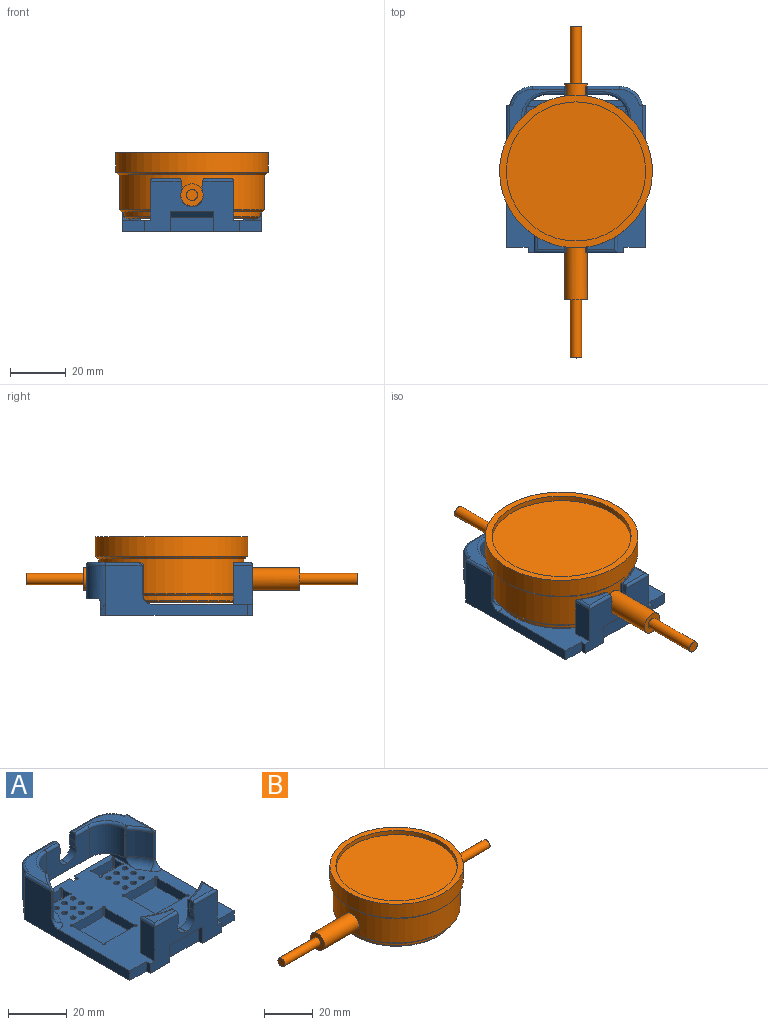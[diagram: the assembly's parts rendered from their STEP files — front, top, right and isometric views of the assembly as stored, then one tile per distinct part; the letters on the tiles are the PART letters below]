
ASSEMBLY  parts=2 mates=1
PART A: 181 faces, bbox 61.3x61.3x19.5 mm
  f0: plane 7x2mm, normal (-1,0,0), area 12mm2, adj f1,f6,f11,f135
  f1: plane 15.6x5mm, normal (0,-1,0), area 78mm2, adj f0,f7,f11,f135
  f2: plane 54.8x50mm, normal (0,0,1), area 1669.8mm2, adj f3,f4,f5,f6,f8,f9,f12,f32
  f3: plane 50.8x18mm, normal (-1,0,0), area 387.9mm2, adj f2,f4,f10,f11,f138,f142,f165
  f4: plane 7.8x4mm, normal (0,-1,0), area 31.2mm2, adj f2,f3,f5,f11
  f5: plane 4x2mm, normal (-1,0,0), area 8mm2, adj f2,f4,f6,f11
  f6: plane 34.4x18mm, normal (0,-1,0), area 383.7mm2, adj f0,f2,f5,f7,f11,f61,f113,f117
  f7: plane 7x2mm, normal (1,0,0), area 12mm2, adj f1,f6,f11,f135
  f8: plane 4.3x4mm, normal (0,1,0), area 13.2mm2, adj f2,f11,f12,f64
  f9: plane 22.09x5mm, normal (0,1,0), area 90.6mm2, adj f2,f11,f12,f13,f125,f153,f174
  f10: plane 19.09x2.26mm, normal (0,1,0), area 23.9mm2, adj f3,f11,f13,f123,f153,f165,f171
  f11: plane 54.8x50mm, normal (0,0,-1), area 2572mm2, adj f0,f1,f3,f4,f5,f6,f7,f8
  f12: plane 4x2mm, normal (0.97,0,-0.24), area 8.2mm2, adj f2,f8,f9,f11
  f13: plane 4x2mm, normal (-0.97,0,-0.24), area 6.1mm2, adj f9,f10,f11,f153
  f14: cylinder r=1.25mm len=2.5mm, axis (0,0,-1), area 11.8mm2, adj f11,f15
  f15: plane 2.5x2.5mm, normal (0,0,-1), area 1.8mm2, adj f14,f40
  f16: cylinder r=1.25mm len=2.5mm, axis (0,0,-1), area 11.8mm2, adj f11,f17
  f17: plane 2.5x2.5mm, normal (0,0,-1), area 1.8mm2, adj f16,f39
  f18: cylinder r=1.25mm len=2.5mm, axis (0,0,-1), area 11.8mm2, adj f11,f19
  f19: plane 2.5x2.5mm, normal (0,0,-1), area 1.8mm2, adj f18,f38
  f20: cylinder r=1.25mm len=2.5mm, axis (0,0,-1), area 11.8mm2, adj f11,f21
  f21: plane 2.5x2.5mm, normal (0,0,-1), area 1.8mm2, adj f20,f37
  f22: cylinder r=1.25mm len=2.5mm, axis (0,0,-1), area 11.8mm2, adj f11,f23
  f23: plane 2.5x2.5mm, normal (0,0,-1), area 1.8mm2, adj f22,f36
  f24: cylinder r=1.25mm len=2.5mm, axis (0,0,-1), area 11.8mm2, adj f11,f25
  f25: plane 2.5x2.5mm, normal (0,0,-1), area 1.8mm2, adj f24,f35
  f26: cylinder r=1.25mm len=2.5mm, axis (0,0,-1), area 11.8mm2, adj f11,f27
  f27: plane 2.5x2.5mm, normal (0,0,-1), area 1.8mm2, adj f26,f34
  f28: cylinder r=1.25mm len=2.5mm, axis (0,0,-1), area 11.8mm2, adj f11,f29
  f29: plane 2.5x2.5mm, normal (0,0,-1), area 1.8mm2, adj f28,f33
  f30: cylinder r=1.25mm len=2.5mm, axis (0,0,-1), area 11.8mm2, adj f11,f31
  f31: plane 2.5x2.5mm, normal (0,0,-1), area 1.8mm2, adj f30,f32
  f32: cylinder r=1mm len=2.5mm, axis (0,0,-1), area 15.7mm2, adj f2,f31
  f33: cylinder r=1mm len=2.5mm, axis (0,0,-1), area 15.7mm2, adj f2,f29
  f34: cylinder r=1mm len=2.5mm, axis (0,0,-1), area 15.7mm2, adj f2,f27
  f35: cylinder r=1mm len=2.5mm, axis (0,0,-1), area 15.7mm2, adj f2,f25
  f36: cylinder r=1mm len=2.5mm, axis (0,0,-1), area 15.7mm2, adj f2,f23
  f37: cylinder r=1mm len=2.5mm, axis (0,0,-1), area 15.7mm2, adj f2,f21
  f38: cylinder r=1mm len=2.5mm, axis (0,0,-1), area 15.7mm2, adj f2,f19
  f39: cylinder r=1mm len=2.5mm, axis (0,0,-1), area 15.7mm2, adj f2,f17
  f40: cylinder r=1mm len=2.5mm, axis (0,0,-1), area 15.7mm2, adj f2,f15
  f41: cylinder r=0.5mm len=3.8mm, axis (0,0,1), area 9mm2, adj f2,f42,f48,f49
  f42: plane 9.35x3.8mm, normal (0,1,0), area 35.5mm2, adj f2,f41,f43,f49
  f43: cylinder r=0.5mm len=3.8mm, axis (0,0,1), area 9mm2, adj f2,f42,f44,f49
  f44: plane 3.8x3.35mm, normal (-1,0,0), area 12.7mm2, adj f2,f43,f45,f49
  f45: cylinder r=0.5mm len=3.8mm, axis (0,0,1), area 9mm2, adj f2,f44,f46,f49
  f46: plane 9.35x3.8mm, normal (0,-1,0), area 35.5mm2, adj f2,f45,f47,f49
  f47: cylinder r=0.5mm len=3.8mm, axis (0,0,1), area 9mm2, adj f2,f46,f48,f49
  f48: plane 3.8x3.35mm, normal (1,0,0), area 12.7mm2, adj f2,f41,f47,f49
  f49: plane 11.35x5.35mm, normal (0,0,1), area 47.4mm2, adj f41,f42,f43,f44,f45,f46,f47,f48
  f50: cylinder r=0.5mm len=3.8mm, axis (0,0,1), area 9mm2, adj f2,f51,f57,f58
  f51: plane 14.35x3.8mm, normal (1,0,0), area 54.5mm2, adj f2,f50,f52,f58
  f52: cylinder r=0.5mm len=3.8mm, axis (0,0,1), area 9mm2, adj f2,f51,f53,f58
  f53: plane 14.35x3.8mm, normal (0,1,0), area 54.5mm2, adj f2,f52,f54,f58
  f54: cylinder r=0.5mm len=3.8mm, axis (0,0,1), area 9mm2, adj f2,f53,f55,f58
  f55: plane 14.35x3.8mm, normal (-1,0,0), area 54.5mm2, adj f2,f54,f56,f58
  f56: cylinder r=0.5mm len=3.8mm, axis (0,0,1), area 9mm2, adj f2,f55,f57,f58
  f57: plane 14.35x3.8mm, normal (0,-1,0), area 54.5mm2, adj f2,f50,f56,f58
  f58: plane 16.35x16.35mm, normal (0,0,1), area 238mm2, adj f50,f51,f52,f53,f54,f55,f56,f57
  f59: plane 50.8x18mm, normal (1,0,0), area 387.9mm2, adj f2,f11,f60,f63,f137,f140,f158
  f60: plane 7.8x4mm, normal (0,-1,0), area 31.2mm2, adj f2,f11,f59,f61
  f61: plane 4x2mm, normal (1,0,0), area 8mm2, adj f2,f6,f11,f60
  f62: plane 22.09x5mm, normal (0,1,0), area 90.6mm2, adj f2,f11,f64,f65,f122,f154,f173
  f63: plane 19.09x2.26mm, normal (0,1,0), area 23.9mm2, adj f11,f59,f65,f120,f154,f158,f169
  f64: plane 4x2mm, normal (-0.97,0,-0.24), area 8.2mm2, adj f2,f8,f11,f62
  f65: plane 4x2mm, normal (0.97,0,-0.24), area 6.1mm2, adj f11,f62,f63,f154
  f66: cylinder r=1.25mm len=2.5mm, axis (0,0,-1), area 11.8mm2, adj f11,f67
  f67: plane 2.5x2.5mm, normal (0,0,-1), area 1.8mm2, adj f66,f92
  f68: cylinder r=1.25mm len=2.5mm, axis (0,0,-1), area 11.8mm2, adj f11,f69
  f69: plane 2.5x2.5mm, normal (0,0,-1), area 1.8mm2, adj f68,f91
  f70: cylinder r=1.25mm len=2.5mm, axis (0,0,-1), area 11.8mm2, adj f11,f71
  f71: plane 2.5x2.5mm, normal (0,0,-1), area 1.8mm2, adj f70,f90
  f72: cylinder r=1.25mm len=2.5mm, axis (0,0,-1), area 11.8mm2, adj f11,f73
  f73: plane 2.5x2.5mm, normal (0,0,-1), area 1.8mm2, adj f72,f89
  f74: cylinder r=1.25mm len=2.5mm, axis (0,0,-1), area 11.8mm2, adj f11,f75
  f75: plane 2.5x2.5mm, normal (0,0,-1), area 1.8mm2, adj f74,f88
  f76: cylinder r=1.25mm len=2.5mm, axis (0,0,-1), area 11.8mm2, adj f11,f77
  f77: plane 2.5x2.5mm, normal (0,0,-1), area 1.8mm2, adj f76,f87
  f78: cylinder r=1.25mm len=2.5mm, axis (0,0,-1), area 11.8mm2, adj f11,f79
  f79: plane 2.5x2.5mm, normal (0,0,-1), area 1.8mm2, adj f78,f86
  f80: cylinder r=1.25mm len=2.5mm, axis (0,0,-1), area 11.8mm2, adj f11,f81
  f81: plane 2.5x2.5mm, normal (0,0,-1), area 1.8mm2, adj f80,f85
  f82: cylinder r=1.25mm len=2.5mm, axis (0,0,-1), area 11.8mm2, adj f11,f83
  f83: plane 2.5x2.5mm, normal (0,0,-1), area 1.8mm2, adj f82,f84
  f84: cylinder r=1mm len=2.5mm, axis (0,0,-1), area 15.7mm2, adj f2,f83
  f85: cylinder r=1mm len=2.5mm, axis (0,0,-1), area 15.7mm2, adj f2,f81
  f86: cylinder r=1mm len=2.5mm, axis (0,0,-1), area 15.7mm2, adj f2,f79
  f87: cylinder r=1mm len=2.5mm, axis (0,0,-1), area 15.7mm2, adj f2,f77
  f88: cylinder r=1mm len=2.5mm, axis (0,0,-1), area 15.7mm2, adj f2,f75
  f89: cylinder r=1mm len=2.5mm, axis (0,0,-1), area 15.7mm2, adj f2,f73
  f90: cylinder r=1mm len=2.5mm, axis (0,0,-1), area 15.7mm2, adj f2,f71
  f91: cylinder r=1mm len=2.5mm, axis (0,0,-1), area 15.7mm2, adj f2,f69
  f92: cylinder r=1mm len=2.5mm, axis (0,0,-1), area 15.7mm2, adj f2,f67
  f93: cylinder r=0.5mm len=3.8mm, axis (0,0,1), area 9mm2, adj f2,f94,f100,f101
  f94: plane 9.35x3.8mm, normal (0,1,0), area 35.5mm2, adj f2,f93,f95,f101
  f95: cylinder r=0.5mm len=3.8mm, axis (0,0,1), area 9mm2, adj f2,f94,f96,f101
  f96: plane 3.8x3.35mm, normal (1,0,0), area 12.7mm2, adj f2,f95,f97,f101
  f97: cylinder r=0.5mm len=3.8mm, axis (0,0,1), area 9mm2, adj f2,f96,f98,f101
  f98: plane 9.35x3.8mm, normal (0,-1,0), area 35.5mm2, adj f2,f97,f99,f101
  f99: cylinder r=0.5mm len=3.8mm, axis (0,0,1), area 9mm2, adj f2,f98,f100,f101
  f100: plane 3.8x3.35mm, normal (-1,0,0), area 12.7mm2, adj f2,f93,f99,f101
  f101: plane 11.35x5.35mm, normal (0,0,1), area 47.4mm2, adj f93,f94,f95,f96,f97,f98,f99,f100
  f102: cylinder r=0.5mm len=3.8mm, axis (0,0,1), area 9mm2, adj f2,f103,f109,f110
  f103: plane 14.35x3.8mm, normal (-1,0,0), area 54.5mm2, adj f2,f102,f104,f110
  f104: cylinder r=0.5mm len=3.8mm, axis (0,0,1), area 9mm2, adj f2,f103,f105,f110
  f105: plane 14.35x3.8mm, normal (0,1,0), area 54.5mm2, adj f2,f104,f106,f110
  f106: cylinder r=0.5mm len=3.8mm, axis (0,0,1), area 9mm2, adj f2,f105,f107,f110
  f107: plane 14.35x3.8mm, normal (1,0,0), area 54.5mm2, adj f2,f106,f108,f110
  f108: cylinder r=0.5mm len=3.8mm, axis (0,0,1), area 9mm2, adj f2,f107,f109,f110
  f109: plane 14.35x3.8mm, normal (0,-1,0), area 54.5mm2, adj f2,f102,f108,f110
  f110: plane 16.35x16.35mm, normal (0,0,1), area 238mm2, adj f102,f103,f104,f105,f106,f107,f108,f109
  f111: cylinder r=26.2mm len=27.83mm, axis (0,0,-1), area 254.8mm2, adj f112,f114,f116,f118,f126,f127,f128,f136
  f112: plane 14.79x8.26mm, normal (0,1,0), area 19.8mm2, adj f2,f111,f113,f136,f178,f180
  f113: plane 14x7mm, normal (-1,0,0), area 98mm2, adj f2,f6,f112,f180
  f114: plane 6.26x1.38mm, normal (1,0,0), area 7.9mm2, adj f111,f115,f127,f134,f178
  f115: plane 9.95x4.88mm, normal (0,0,1), area 27.1mm2, adj f114,f133,f178,f179,f180
  f116: plane 6.26x1.38mm, normal (-1,0,0), area 7.9mm2, adj f111,f119,f128,f129,f175
  f117: plane 14x7mm, normal (1,0,0), area 98mm2, adj f2,f6,f118,f177
  f118: plane 14.79x8.26mm, normal (0,1,0), area 19.8mm2, adj f2,f111,f117,f136,f175,f177
  f119: plane 9.95x4.88mm, normal (0,0,1), area 27.1mm2, adj f116,f130,f175,f176,f177
  f120: plane 19.95x16.8mm, normal (0,0,1), area 75.3mm2, adj f63,f151,f157,f158,f159,f161,f162,f169
  f121: cylinder r=26.2mm len=11mm, axis (0,0,-1), area 106.2mm2, adj f122,f137,f139,f162
  f122: plane 14x12.83mm, normal (-1,0,0), area 26.8mm2, adj f2,f62,f121,f139,f143,f156,f161,f173
  f123: plane 19.95x16.8mm, normal (0,0,1), area 75.3mm2, adj f10,f145,f163,f164,f165,f166,f168,f171
  f124: cylinder r=26.2mm len=11mm, axis (0,0,-1), area 106.2mm2, adj f125,f138,f141,f168
  f125: plane 14x12.83mm, normal (1,0,0), area 26.8mm2, adj f2,f9,f124,f141,f143,f155,f166,f174
  f126: plane 3x0.1mm, normal (0,0,1), area 0.3mm2, adj f6,f111,f127,f128
  f127: cylinder r=4mm len=4mm, axis (0,1,0), area 19.8mm2, adj f6,f111,f114,f126,f132
  f128: cylinder r=4mm len=4mm, axis (0,-1,0), area 19.8mm2, adj f6,f111,f116,f126,f131
  f129: plane 6.2x0.5mm, normal (0,1,0), area 1.5mm2, adj f116,f130,f131
  f130: plane 3.07x2.07mm, normal (-0.99,0,0.16), area 5.9mm2, adj f6,f119,f129,f131,f176
  f131: plane 3.2x2mm, normal (-0.99,0,-0.15), area 6.5mm2, adj f6,f128,f129,f130
  f132: plane 3.2x2mm, normal (0.99,0,-0.15), area 6.5mm2, adj f6,f127,f133,f134
  f133: plane 3.07x2.07mm, normal (0.99,0,0.16), area 5.9mm2, adj f6,f115,f132,f134,f179
  f134: plane 6.2x0.5mm, normal (0,1,0), area 1.6mm2, adj f114,f132,f133
  f135: plane 15.6x2mm, normal (0,-0.71,-0.71), area 44.1mm2, adj f0,f1,f6,f7
  f136: torus R=23.2mm, axis (0,0,1), area 113.8mm2, adj f2,f111,f112,f118
  f137: cylinder r=0.5mm len=11mm, axis (0,0,-1), area 15mm2, adj f59,f121,f140,f160
  f138: cylinder r=0.5mm len=11mm, axis (0,0,-1), area 15mm2, adj f3,f124,f142,f167
  f139: torus R=23.2mm, axis (0,0,1), area 38.1mm2, adj f2,f121,f122,f140
  f140: torus R=3.5mm, axis (0,0,1), area 11.3mm2, adj f2,f59,f137,f139
  f141: torus R=23.2mm, axis (0,0,1), area 38.1mm2, adj f2,f124,f125,f142
  f142: torus R=3.5mm, axis (0,0,1), area 11.3mm2, adj f2,f3,f138,f141
  f143: plane 45.42x11.45mm, normal (0,0,-1), area 158.1mm2, adj f122,f125,f144,f152,f153,f154,f155,f156
  f144: plane 20.45x12mm, normal (0,-1,0), area 180.7mm2, adj f143,f145,f146,f147,f148,f149,f150,f151
  f145: plane 3.07x3.07mm, normal (0.99,0,0.16), area 8.7mm2, adj f123,f144,f146,f152,f163,f172
  f146: plane 3.2x3mm, normal (0.99,0,-0.15), area 9.7mm2, adj f144,f145,f147,f152
  f147: cylinder r=4mm len=4mm, axis (0,-1,0), area 18.8mm2, adj f144,f146,f148,f152
  f148: plane 3x0.1mm, normal (0,0,1), area 0.3mm2, adj f144,f147,f149,f152
  f149: cylinder r=4mm len=4mm, axis (0,-1,0), area 18.8mm2, adj f144,f148,f150,f152
  f150: plane 3.2x3mm, normal (-0.99,0,-0.15), area 9.7mm2, adj f144,f149,f151,f152
  f151: plane 3.07x3.07mm, normal (-0.99,0,0.16), area 8.7mm2, adj f120,f144,f150,f152,f157,f170
  f152: plane 31.05x12mm, normal (0,1,0), area 307.9mm2, adj f143,f145,f146,f147,f148,f149,f150,f151
  f153: cylinder r=8.45mm len=16.44mm, axis (0,0,1), area 148.4mm2, adj f9,f10,f13,f143,f152,f171,f174
  f154: cylinder r=8.45mm len=16.44mm, axis (0,0,1), area 148.4mm2, adj f62,f63,f65,f143,f152,f169,f173
  f155: cylinder r=8.45mm len=12mm, axis (0,0,-1), area 159.3mm2, adj f125,f143,f144,f164
  f156: cylinder r=8.45mm len=12mm, axis (0,0,-1), area 159.3mm2, adj f122,f143,f144,f159
  f157: cylinder r=1mm len=6.34mm, axis (1,0,0), area 9.8mm2, adj f120,f144,f151,f159
  f158: cylinder r=1mm len=12.99mm, axis (0,1,0), area 19.1mm2, adj f59,f63,f120,f160
  f159: torus R=9.45mm, axis (0,0,1), area 21.7mm2, adj f120,f156,f157,f161
  f160: bspline ~4.6x2mm, area 2.1mm2, adj f137,f158,f162
  f161: cylinder r=1mm len=1mm, axis (0,1,0), area 1mm2, adj f120,f122,f159,f162
  f162: torus R=27.2mm, axis (0,0,1), area 13.9mm2, adj f120,f121,f160,f161
  f163: cylinder r=1mm len=6.34mm, axis (1,0,0), area 9.8mm2, adj f123,f144,f145,f164
  f164: torus R=9.45mm, axis (0,0,1), area 21.7mm2, adj f123,f155,f163,f166
  f165: cylinder r=1mm len=12.99mm, axis (0,1,0), area 19.1mm2, adj f3,f10,f123,f167
  f166: cylinder r=1mm len=1mm, axis (0,-1,0), area 1mm2, adj f123,f125,f164,f168
  f167: bspline ~4.6x2mm, area 2.1mm2, adj f138,f165,f168
  f168: torus R=27.2mm, axis (0,0,1), area 13.9mm2, adj f123,f124,f166,f167
  f169: torus R=7.45mm, axis (0,0,1), area 17.6mm2, adj f63,f120,f154,f170
  f170: cylinder r=1mm len=11.64mm, axis (-1,0,0), area 18.2mm2, adj f120,f151,f152,f169
  f171: torus R=7.45mm, axis (0,0,1), area 17.6mm2, adj f10,f123,f153,f172
  f172: cylinder r=1mm len=11.64mm, axis (-1,0,0), area 18.2mm2, adj f123,f145,f152,f171
  f173: cylinder r=1mm len=4.56mm, axis (-1,0,0), area 6.9mm2, adj f62,f122,f143,f154
  f174: cylinder r=1mm len=4.56mm, axis (-1,0,0), area 6.9mm2, adj f9,f125,f143,f153
  f175: torus R=27.2mm, axis (0,0,1), area 17.2mm2, adj f111,f116,f118,f119,f177
  f176: cylinder r=1mm len=11.12mm, axis (1,0,0), area 16.8mm2, adj f6,f119,f130,f177
  f177: cylinder r=1mm len=7mm, axis (0,-1,0), area 10.1mm2, adj f117,f118,f119,f175,f176
  f178: torus R=27.2mm, axis (0,0,1), area 17.2mm2, adj f111,f112,f114,f115,f180
  f179: cylinder r=1mm len=11.12mm, axis (-1,0,0), area 16.8mm2, adj f6,f115,f133,f180
  f180: cylinder r=1mm len=7mm, axis (0,1,0), area 10.1mm2, adj f112,f113,f115,f178,f179
PART B: 20 faces, bbox 119.3x54.9x23.8 mm
  f0: cylinder r=26.1mm len=52.2mm, axis (0,0,-1), area 1948.8mm2, adj f5,f6,f8,f16
  f1: cylinder r=24.5mm len=49mm, axis (0,0,-1), area 261.7mm2, adj f3,f9
  f2: plane 47.4x47.4mm, normal (0,0,-1), area 1764.6mm2, adj f9
  f3: plane 50.6x50.6mm, normal (0,0,-1), area 125.2mm2, adj f1,f8
  f4: plane 8x8mm, normal (1,0,0), area 37.7mm2, adj f5,f12
  f5: cylinder r=4mm len=8mm, axis (-1,0,0), area 139.6mm2, adj f0,f4
  f6: cylinder r=4mm len=20.21mm, axis (-1,0,0), area 504mm2, adj f0,f7
  f7: plane 8x8mm, normal (-1,0,0), area 37.7mm2, adj f6,f11
  f8: cone r=26.1mm half-angle=45deg, axis (0,0,1), area 182.7mm2, adj f0,f3
  f9: cone r=24.5mm half-angle=45deg, axis (0,0,1), area 171.3mm2, adj f1,f2
  f10: plane 4x4mm, normal (-1,0,0), area 12.6mm2, adj f11
  f11: cylinder r=2mm len=21mm, axis (-1,0,0), area 263.9mm2, adj f7,f10
  f12: cylinder r=2mm len=20.8mm, axis (-1,0,0), area 261.4mm2, adj f4,f13
  f13: plane 4x4mm, normal (1,0,0), area 12.6mm2, adj f12
  f14: cylinder r=27.45mm len=54.9mm, axis (0,0,-1), area 1207.3mm2, adj f15,f19
  f15: plane 54.9x54.9mm, normal (0,0,1), area 403.7mm2, adj f14,f17
  f16: plane 52.9x52.9mm, normal (0,0,-1), area 57.8mm2, adj f0,f19
  f17: cylinder r=25mm len=50mm, axis (0,0,1), area 314.2mm2, adj f15,f18
  f18: plane 50x50mm, normal (0,0,1), area 1963.5mm2, adj f17
  f19: cone r=27.45mm half-angle=45deg, axis (0,0,1), area 239.5mm2, adj f14,f16
PLACE A t=(-44.97,-46.34,-11.29)mm
PLACE B rot(axis=(0,0,1),90deg) t=(-19.97,-19.14,-6.84)mm
MATE slider B.f0 <-> A.f111  axis (0,0,-1) through (-19.97,-19.14,2.71)mm
